# Revit family: Magnuson-Dacapo-Free_Standing
name_source: partatom
category: Furniture
revit_build: Autodesk Revit 2016 (Build: 20150220_1215(x64)
units: mm (PartAtom-declared; Revit-internal decimal feet)

## family parameters
Always vertical = Yes
Cut with Voids When Loaded = No
OmniClass Number = 23.40.20.00
OmniClass Title = General Furniture and Specialties
Room Calculation Point = No
Shared = No
Work Plane-Based = No

## types (1)
- DACI-PR
    Assembly Code = E2020200
    Base Finish = MAG - Paint Steel Coat Black
    Cap Finish = MAG - Aluminum Pearl Grey
    Depth = 13 1/16"
    Description = Free standing double sided display with 9 slots on each side
    Display Finish = MAG - Paint Steel Coat Black
    Frame Finish = MAG - Aluminum Pearl Grey
    Height = 68 1/8"
    Keynote = 12500
    Low Emitting Finish = Yes
    Low Emitting Material = Yes
    Manufacturer = MAGNUSON
    Model = DACI-PR
    Percentage of Recycled Content = 0
    Salvage or Reuse = Yes
    Type Comments = DACAPO
    URL = www.magnusongroup.com
    Width = 13 1/16"

## geometry (parser evidence)
native form markers: Sweep x2
no freeform markers — native parametric forms only
